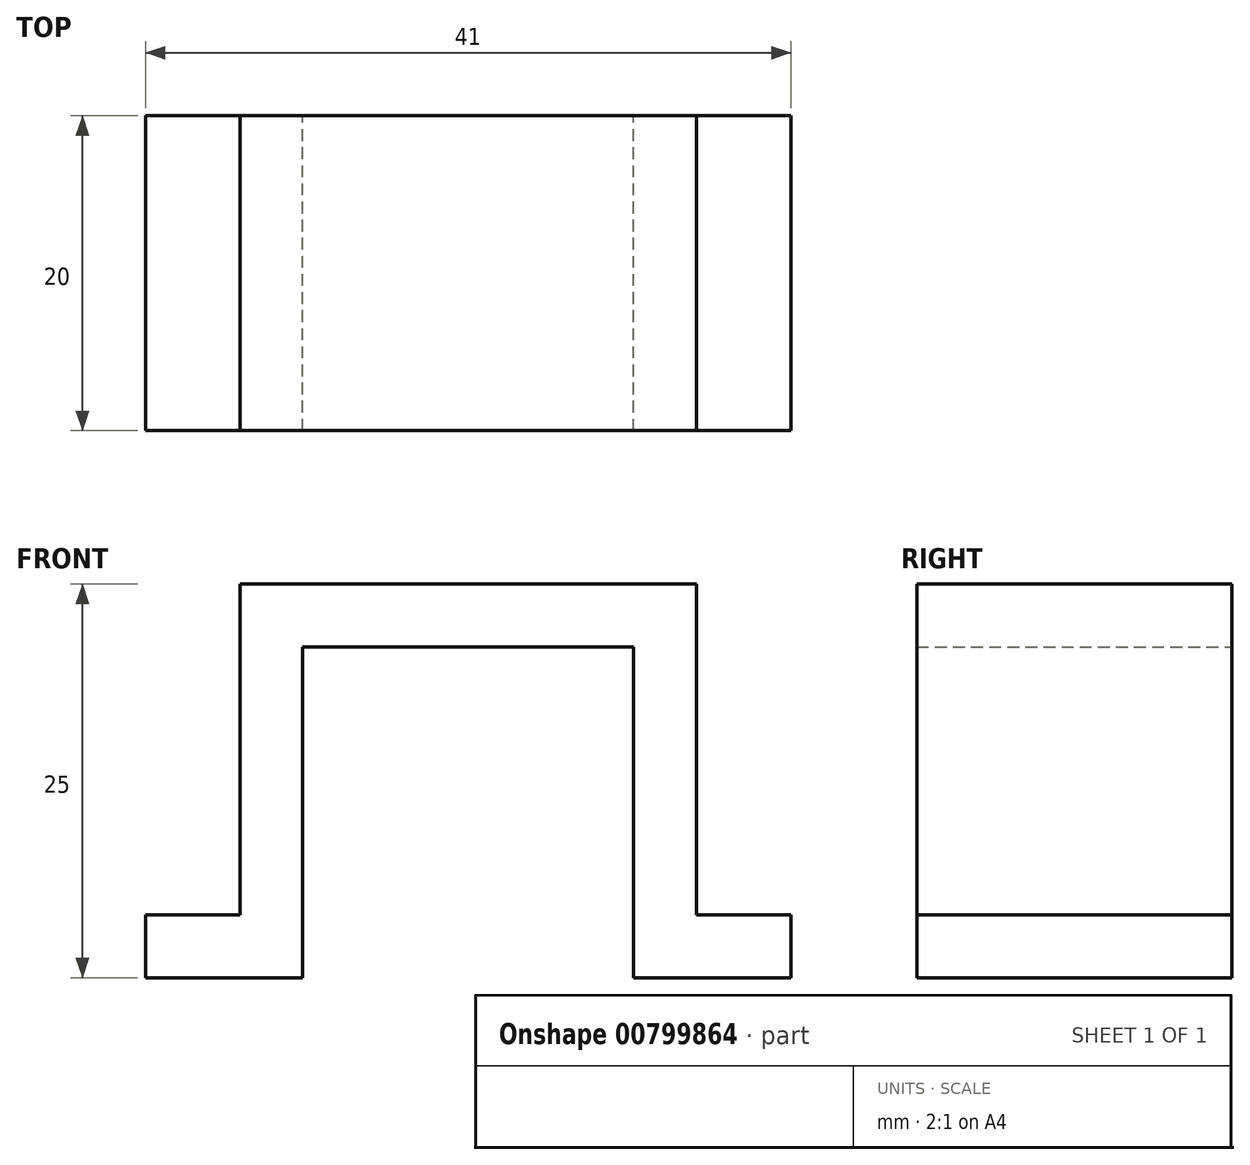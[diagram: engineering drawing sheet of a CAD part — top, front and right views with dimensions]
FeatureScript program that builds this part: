
annotation { "Feature Type Name" : "Feature", "Feature Type Description" : "" }
export const myFeature = defineFeature(function(context is Context, id is Id, definition is map)
    precondition{}
    {
        {
            var Q0;
            Q0=qCreatedBy(makeId("Front.planeOp"),FACE);
            var sketch = newSketch(context, id + "F0", { "sketchPlane" : qUnion([Q0])});
            skLineSegment(sketch, "E0.top", {"start": v(0, 21) * mm, "end": v(21, 21) * mm});
            skLineSegment(sketch, "E0.left", {"start": v(0, 0) * mm, "end": v(0, 21) * mm});
            skLineSegment(sketch, "E0.right", {"start": v(21, 0) * mm, "end": v(21, 21) * mm});
            skLineSegment(sketch, "E1.bottom", {"start": v(21, 0) * mm, "end": v(25, 0) * mm});
            skLineSegment(sketch, "E1.top", {"start": v(0, 25) * mm, "end": v(25, 25) * mm});
            skLineSegment(sketch, "E1.right", {"start": v(25, 4) * mm, "end": v(25, 25) * mm});
            skLineSegment(sketch, "E2.bottom", {"start": v(0, 0) * mm, "end": v(-4, 0) * mm});
            skLineSegment(sketch, "E2.top", {"start": v(0, 25) * mm, "end": v(-4, 25) * mm});
            skLineSegment(sketch, "E2.right", {"start": v(-4, 4) * mm, "end": v(-4, 25) * mm});
            skLineSegment(sketch, "E3.bottom", {"start": v(0, 0) * mm, "end": v(-10, 0) * mm});
            skLineSegment(sketch, "E3.top", {"start": v(-4, 4) * mm, "end": v(-10, 4) * mm});
            skLineSegment(sketch, "E3.left", {"start": v(0, 0) * mm, "end": v(0, 4) * mm});
            skLineSegment(sketch, "E3.right", {"start": v(-10, 0) * mm, "end": v(-10, 4) * mm});
            skLineSegment(sketch, "E4.bottom", {"start": v(21, 0) * mm, "end": v(31, 0) * mm});
            skLineSegment(sketch, "E4.top", {"start": v(25, 4) * mm, "end": v(31, 4) * mm});
            skLineSegment(sketch, "E4.left", {"start": v(21, 0) * mm, "end": v(21, 4) * mm});
            skLineSegment(sketch, "E4.right", {"start": v(31, 0) * mm, "end": v(31, 4) * mm});
            skSolve(sketch);
        }
        {
            var Q0;
            Q0=makeQuery(id+"F0.imprint","IMPRINT",FACE,{"disambiguationData":[TD([[makeQuery(id+"F0.imprint","IMPRINT",EDGE,{"derivedFrom":sQuery(id+"F0.wireOp",EDGE,"E0.top")}),1.0]])]});
            extrude(context, id + "F1", {"entities" : qUnion([Q0]), "depth" : 20 * mm, "offsetDistance" : 25 * mm});
        }
    });
